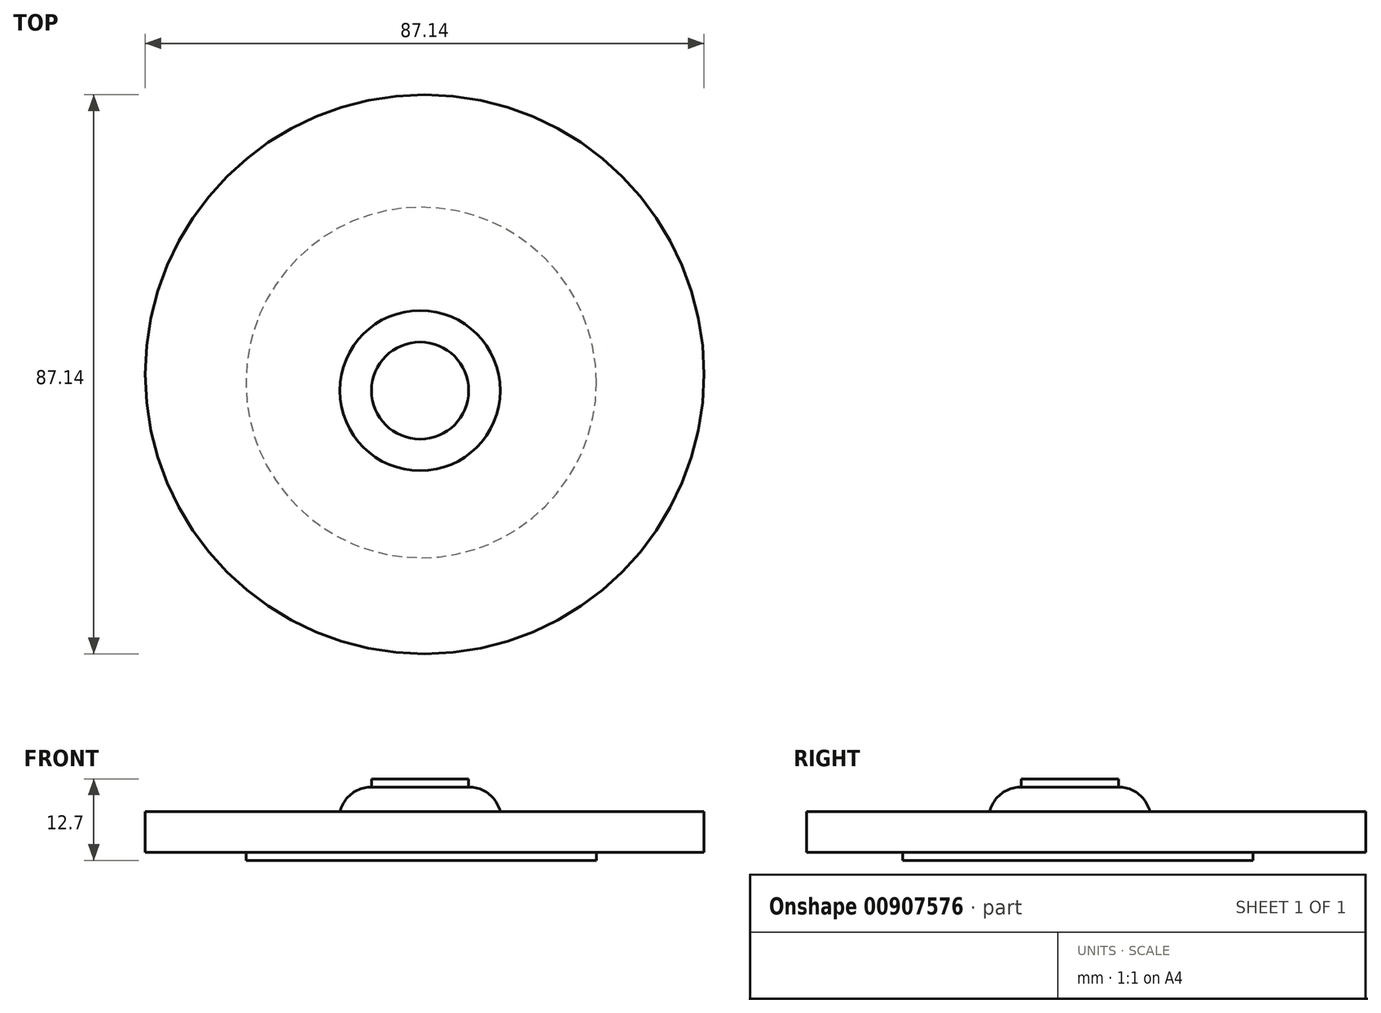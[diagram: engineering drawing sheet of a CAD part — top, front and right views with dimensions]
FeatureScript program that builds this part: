
annotation { "Feature Type Name" : "Feature", "Feature Type Description" : "" }
export const myFeature = defineFeature(function(context is Context, id is Id, definition is map)
    precondition{}
    {
        {
            var Q0;
            Q0=qCreatedBy(makeId("Top.planeOp"),FACE);
            var sketch = newSketch(context, id + "F0", { "sketchPlane" : qUnion([Q0])});
            skCircle(sketch, "E0", {"center": v(0, 0) * mm, "radius": 43.57 * mm});
            skSolve(sketch);
        }
        {
            var Q0;
            Q0 = qSketchRegion(id + "F0", true);
            extrude(context, id + "F1", {"entities" : qUnion([Q0]), "depth" : 6.35 * mm, "offsetDistance" : 25.4 * mm});
        }
        {
            var Q0;
            Q0=makeQuery(id+"F1.opExtrude","CAP_FACE",FACE,{"disambiguationData":[OSD([sQuery(id+"F0.wireOp",EDGE,"E0")])],"isStart":false});
            var sketch = newSketch(context, id + "F2", { "sketchPlane" : qUnion([Q0])});
            skCircle(sketch, "E1", {"center": v(-0.7, -2.55) * mm, "radius": 12.5 * mm});
            skSolve(sketch);
        }
        {
            var Q0;
            Q0 = qSketchRegion(id + "F2", true);
            extrude(context, id + "F3", {"entities" : qUnion([Q0]), "depth" : 3.8 * mm, "offsetDistance" : 25.4 * mm});
        }
        {
            var Q0;
            Q0=makeQuery(id+"F3.opExtrude","CAP_FACE",FACE,{"disambiguationData":[OSD([sQuery(id+"F2.wireOp",EDGE,"E1")])],"isStart":false});
            fillet(context, id + "F4", {"entities" : qUnion([Q0]), "radius" : 5.08 * mm, "tangentPropagation" : true, "allowEdgeOverflow" : false});
        }
        {
            var Q0;
            Q0=qCreatedBy(makeId("Top.planeOp"),FACE);
            var sketch = newSketch(context, id + "F5", { "sketchPlane" : qUnion([Q0])});
            skCircle(sketch, "E2", {"center": v(-0.53, -1.29) * mm, "radius": 27.32 * mm});
            skSolve(sketch);
        }
        {
            var Q0;
            Q0 = qSketchRegion(id + "F5", true);
            extrude(context, id + "F6", {"entities" : qUnion([Q0]), "operationType" : NewBodyOperationType.ADD, "oppositeDirection" : true, "depth" : 1.27 * mm, "offsetDistance" : 25.4 * mm});
        }
        {
            var Q0;
            Q0=makeQuery(id+"F3.opExtrude","CAP_FACE",FACE,{"disambiguationData":[OSD([sQuery(id+"F2.wireOp",EDGE,"E1")])],"isStart":false});
            extrude(context, id + "F7", {"entities" : qUnion([Q0]), "operationType" : NewBodyOperationType.ADD, "depth" : 1.27 * mm, "offsetDistance" : 25.4 * mm});
        }
    });
